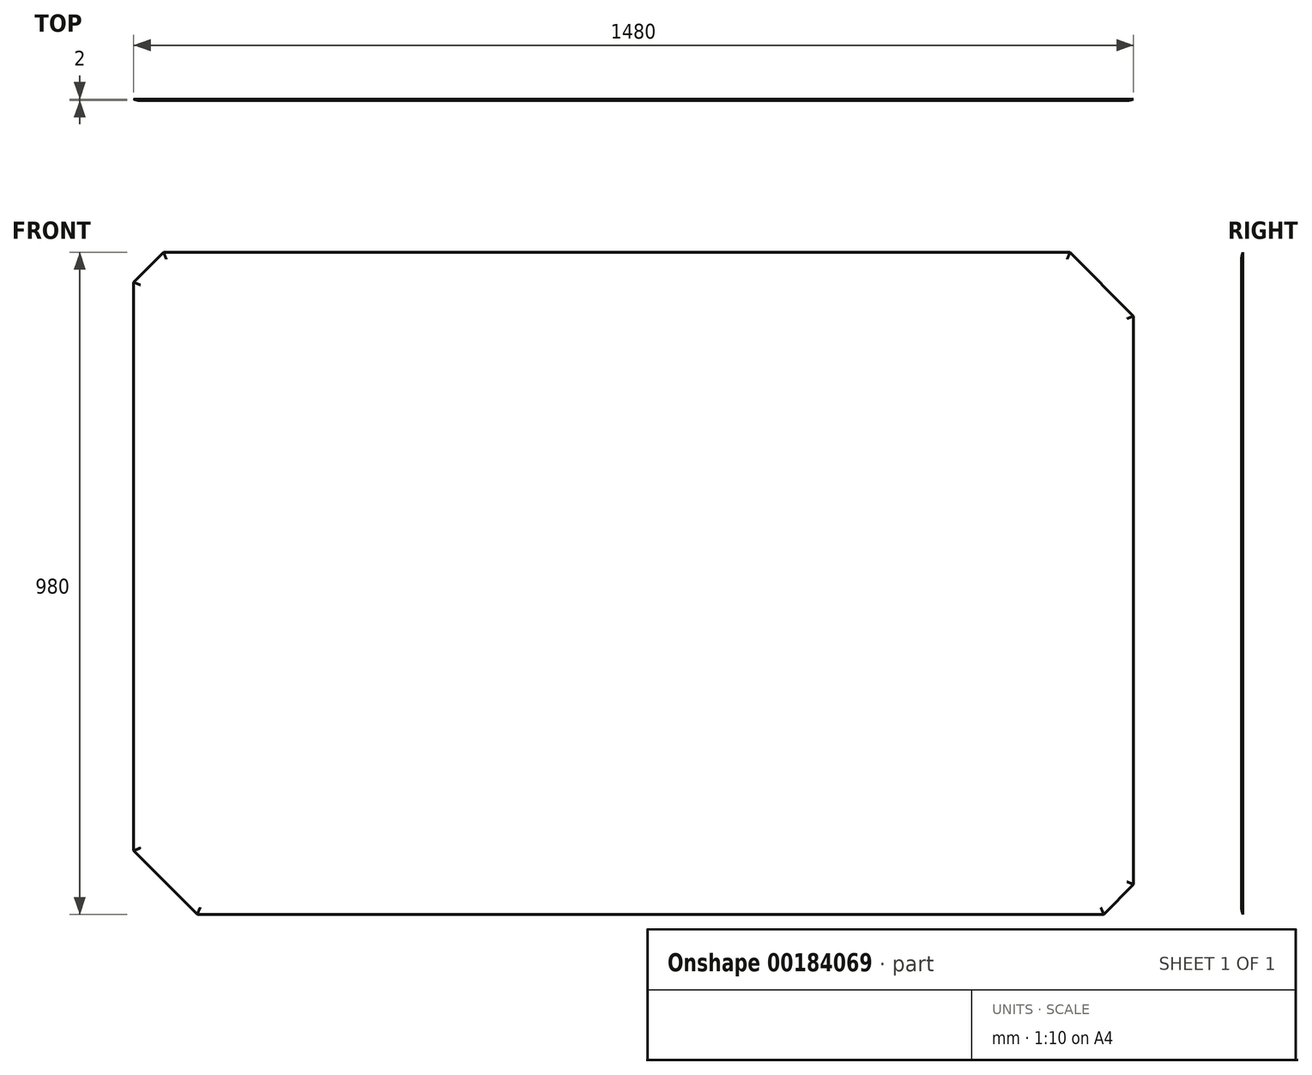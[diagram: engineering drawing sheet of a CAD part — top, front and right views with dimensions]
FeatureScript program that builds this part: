
annotation { "Feature Type Name" : "Feature", "Feature Type Description" : "" }
export const myFeature = defineFeature(function(context is Context, id is Id, definition is map)
    precondition{}
    {
        {
            assignVariable(context, id + "F0", {"name" : "LENGTH", "anyValue" : 2});
        }
        {
            var Q0;
            Q0=qCreatedBy(makeId("Front.planeOp"),FACE);
            var sketch = newSketch(context, id + "F1", { "sketchPlane" : qUnion([Q0])});
            skLineSegment(sketch, "E0.bottom", {"start": v(-750, -500) * mm, "end": v(750, -500) * mm});
            skLineSegment(sketch, "E0.top", {"start": v(-750, 500) * mm, "end": v(750, 500) * mm});
            skLineSegment(sketch, "E0.left", {"start": v(-750, -500) * mm, "end": v(-750, 500) * mm});
            skLineSegment(sketch, "E0.right", {"start": v(750, -500) * mm, "end": v(750, 500) * mm});
            skSolve(sketch);
        }
        {
            var Q0;
            Q0 = qSketchRegion(id + "F1", true);
            extrude(context, id + "F2", {"entities" : qUnion([Q0]), "depth" : (getVariable(context, 'LENGTH') / 2) * mm, "hasSecondDirection" : true, "secondDirectionOppositeDirection" : true, "secondDirectionDepth" : (getVariable(context, 'LENGTH') / 2) * mm});
        }
        {
            var Q0;
            Q0=makeQuery(id+"F2.opExtrude","SWEPT_EDGE",EDGE,{"disambiguationData":[OSD([sQuery(id+"F1.wireOp",EDGE,"E0.bottom"),sQuery(id+"F1.wireOp",EDGE,"E0.right")])]});
            var Q1;
            Q1=makeQuery(id+"F2.opExtrude","SWEPT_EDGE",EDGE,{"disambiguationData":[OSD([sQuery(id+"F1.wireOp",EDGE,"E0.top"),sQuery(id+"F1.wireOp",EDGE,"E0.left")])]});
            chamfer(context, id + "F3", {"entities" : qUnion([Q0, Q1]), "width" : 50 * mm, "tangentPropagation" : true});
        }
        {
            var Q0;
            Q0=makeQuery(id+"F2.opExtrude","SWEPT_EDGE",EDGE,{"disambiguationData":[OSD([sQuery(id+"F1.wireOp",EDGE,"E0.top"),sQuery(id+"F1.wireOp",EDGE,"E0.right")])]});
            var Q1;
            Q1=makeQuery(id+"F2.opExtrude","SWEPT_EDGE",EDGE,{"disambiguationData":[OSD([sQuery(id+"F1.wireOp",EDGE,"E0.bottom"),sQuery(id+"F1.wireOp",EDGE,"E0.left")])]});
            chamfer(context, id + "F4", {"entities" : qUnion([Q0, Q1]), "width" : 100 * mm, "tangentPropagation" : true});
        }
        {
            var Q0;
            Q0=makeQuery(id+"F2.opExtrude","CAP_FACE",FACE,{"disambiguationData":[OSD([sQuery(id+"F1.wireOp",EDGE,"E0.bottom"),sQuery(id+"F1.wireOp",EDGE,"E0.top"),sQuery(id+"F1.wireOp",EDGE,"E0.left"),sQuery(id+"F1.wireOp",EDGE,"E0.right")])],"isStart":true});
            chamfer(context, id + "F5", {"entities" : qUnion([Q0]), "width" : 10 * mm, "tangentPropagation" : true});
        }
        {
            var Q0;
            Q0=makeQuery(id+"F2.opExtrude","CAP_FACE",FACE,{"disambiguationData":[OSD([sQuery(id+"F1.wireOp",EDGE,"E0.bottom"),sQuery(id+"F1.wireOp",EDGE,"E0.top"),sQuery(id+"F1.wireOp",EDGE,"E0.left"),sQuery(id+"F1.wireOp",EDGE,"E0.right")])],"isStart":false});
            fillet(context, id + "F6", {"entities" : qUnion([Q0]), "radius" : 25 * mm, "tangentPropagation" : true, "allowEdgeOverflow" : false});
        }
    });
